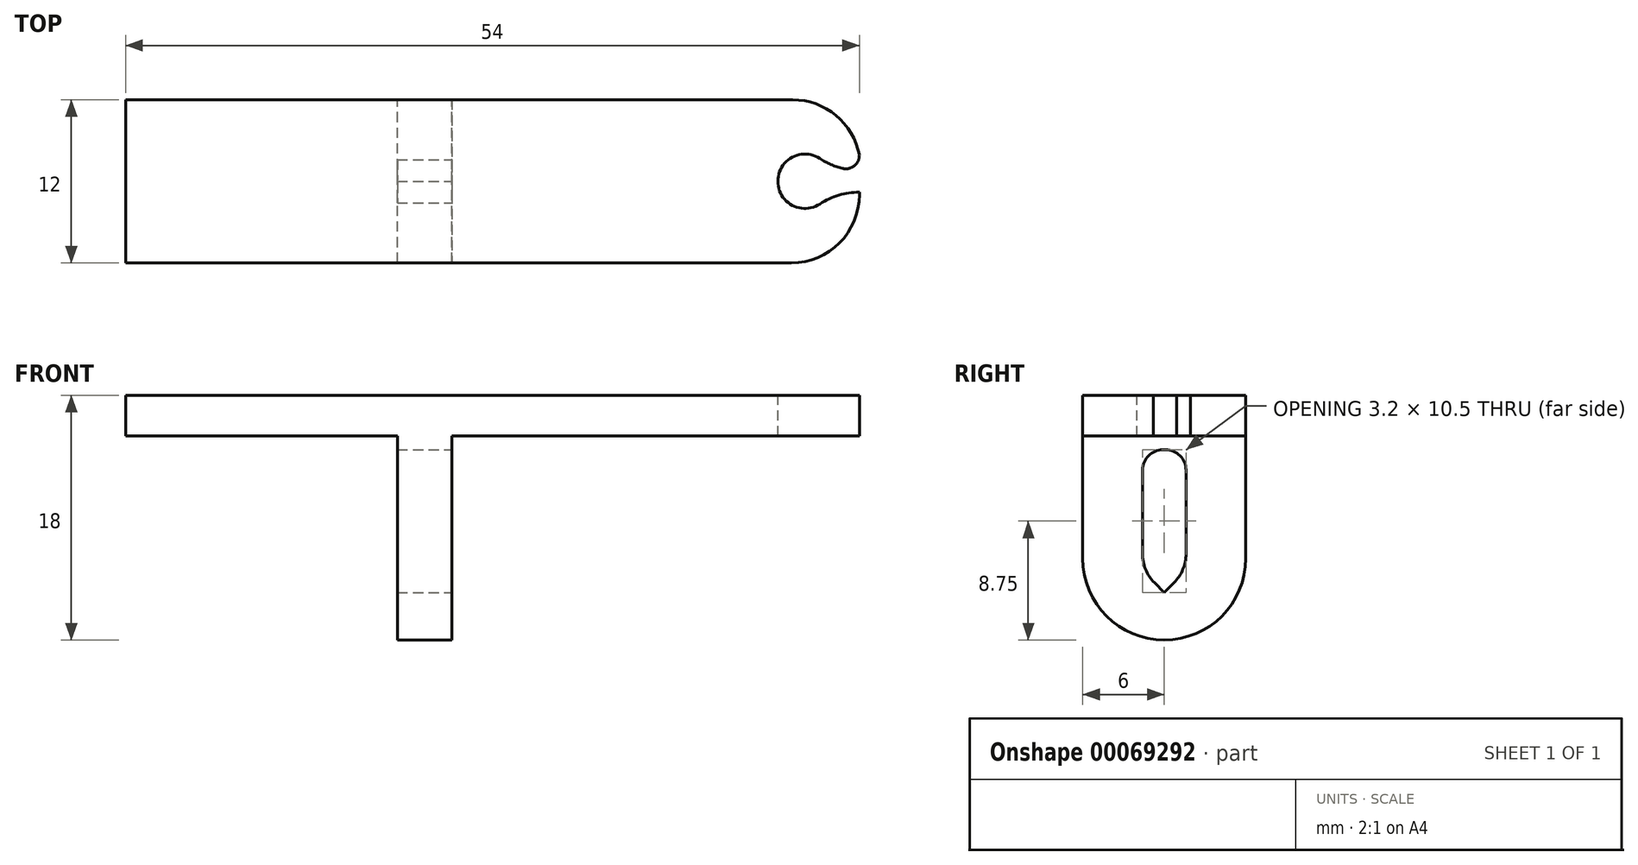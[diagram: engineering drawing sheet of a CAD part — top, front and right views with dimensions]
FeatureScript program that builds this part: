
annotation { "Feature Type Name" : "Feature", "Feature Type Description" : "" }
export const myFeature = defineFeature(function(context is Context, id is Id, definition is map)
    precondition{}
    {
        {
            var Q0;
            Q0=qCreatedBy(makeId("Front.planeOp"),FACE);
            var sketch = newSketch(context, id + "F0", { "sketchPlane" : qUnion([Q0])});
            skLineSegment(sketch, "E0", {"start": v(0, 0) * mm, "end": v(30, 0) * mm});
            skLineSegment(sketch, "E1", {"start": v(30, 0) * mm, "end": v(30, 3) * mm});
            skLineSegment(sketch, "E2", {"start": v(30, 3) * mm, "end": v(-24, 3) * mm});
            skLineSegment(sketch, "E3", {"start": v(-24, 3) * mm, "end": v(-24, 0) * mm});
            skLineSegment(sketch, "E4", {"start": v(-24, 0) * mm, "end": v(-4, 0) * mm});
            skLineSegment(sketch, "E5", {"start": v(-4, 0) * mm, "end": v(-4, -15) * mm});
            skLineSegment(sketch, "E6", {"start": v(-4, -15) * mm, "end": v(0, -15) * mm});
            skLineSegment(sketch, "E7", {"start": v(0, -15) * mm, "end": v(0, 0) * mm});
            skSolve(sketch);
        }
        {
            var Q0;
            Q0=makeQuery(id+"F0.imprint","IMPRINT",FACE,{"disambiguationData":[TD([[makeQuery(id+"F0.imprint","IMPRINT",EDGE,{"derivedFrom":sQuery(id+"F0.wireOp",EDGE,"E0")}),1.0]])]});
            extrude(context, id + "F1", {"entities" : qUnion([Q0]), "endBound" : BoundingType.SYMMETRIC, "depth" : 12 * mm});
        }
        {
            var Q0;
            Q0=makeQuery(id+"F1.opExtrude","SWEPT_FACE",FACE,{"disambiguationData":[OSD([sQuery(id+"F0.wireOp",EDGE,"E2")])]});
            var sketch = newSketch(context, id + "F2", { "sketchPlane" : qUnion([Q0])});
            skArc(sketch, "E8", {"start": v(27.1, 1.67) * mm, "mid": v(24, 0) * mm, "end": v(27.1, -1.67) * mm});
            skArc(sketch, "E9", {"start": v(27.1, 1.67) * mm, "mid": v(28.49, 1.02) * mm, "end": v(30, 0.8) * mm});
            skLineSegment(sketch, "E10.0", {"start": v(30, -0.8) * mm, "end": v(30, 0.8) * mm});
            skArc(sketch, "E11.MirrorCS", {"start": v(27.1, -1.67) * mm, "mid": v(28.49, -1.02) * mm, "end": v(30, -0.8) * mm});
            skPoint(sketch, "E12.orphan", {"position": v(30, 6) * mm});
            skPoint(sketch, "E13.orphan", {"position": v(30, -6) * mm});
            skSolve(sketch);
        }
        {
            var Q0;
            Q0=makeQuery(id+"F2.imprint","IMPRINT",FACE,{"disambiguationData":[TD([[makeQuery(id+"F2.imprint","IMPRINT",EDGE,{"derivedFrom":sQuery(id+"F2.wireOp",EDGE,"E8")}),1.0]])]});
            extrude(context, id + "F3", {"entities" : qUnion([Q0]), "operationType" : NewBodyOperationType.REMOVE, "endBound" : BoundingType.THROUGH_ALL, "oppositeDirection" : true, "depth" : 25 * mm});
        }
        {
            var Q0;
            Q0=makeQuery(id+"F3.boolean.opBoolean","COPY",EDGE,{"derivedFrom":makeQuery(id+"F3.opExtrude","SWEPT_EDGE",EDGE,{"disambiguationData":[OSD([sQuery(id+"F0.wireOp",EDGE,"E1"),sQuery(id+"F0.wireOp",EDGE,"E2"),sQuery(id+"F2.wireOp",EDGE,"E9"),sQuery(id+"F2.wireOp",EDGE,"E10.0")])]})});
            var Q1;
            Q1=makeQuery(id+"F3.boolean.opBoolean","COPY",EDGE,{"derivedFrom":makeQuery(id+"F3.opExtrude","SWEPT_EDGE",EDGE,{"disambiguationData":[OSD([sQuery(id+"F0.wireOp",EDGE,"E1"),sQuery(id+"F0.wireOp",EDGE,"E2"),sQuery(id+"F2.wireOp",EDGE,"E10.0"),sQuery(id+"F2.wireOp",EDGE,"E11.MirrorCS")])]})});
            fillet(context, id + "F4", {"entities" : qUnion([Q0, Q1]), "radius" : 1 * mm, "allowEdgeOverflow" : false});
        }
        {
            var Q0;
            Q0=makeQuery(id+"F1.opExtrude","CAP_EDGE",EDGE,{"disambiguationData":[OSD([sQuery(id+"F0.wireOp",EDGE,"E1")])],"isStart":true});
            var Q1;
            Q1=makeQuery(id+"F1.opExtrude","CAP_EDGE",EDGE,{"disambiguationData":[OSD([sQuery(id+"F0.wireOp",EDGE,"E1")])],"isStart":false});
            fillet(context, id + "F5", {"entities" : qUnion([Q0, Q1]), "radius" : 5 * mm, "tangentPropagation" : true, "allowEdgeOverflow" : false});
        }
        {
            var Q0;
            Q0=makeQuery(id+"F1.opExtrude","SWEPT_FACE",FACE,{"disambiguationData":[OSD([sQuery(id+"F0.wireOp",EDGE,"E7")])]});
            var sketch = newSketch(context, id + "F6", { "sketchPlane" : qUnion([Q0])});
            skLineSegment(sketch, "E14.rect.bottom", {"start": v(-0.1, -1) * mm, "end": v(0.1, -1) * mm});
            skLineSegment(sketch, "E14.rect.left", {"start": v(-1.6, -2.5) * mm, "end": v(-1.6, -9.9) * mm});
            skLineSegment(sketch, "E14.rect.right", {"start": v(1.6, -2.5) * mm, "end": v(1.6, -9.9) * mm});
            skPoint(sketch, "E15", {"position": v(0, -1) * mm});
            skPoint(sketch, "E16.visualSharp", {"position": v(-1.6, -1) * mm});
            skArc(sketch, "E16.filletArc", {"start": v(-0.1, -1) * mm, "mid": v(-1.16, -1.44) * mm, "end": v(-1.6, -2.5) * mm});
            skPoint(sketch, "E17.visualSharp", {"position": v(1.6, -1) * mm});
            skArc(sketch, "E17.filletArc", {"start": v(1.6, -2.5) * mm, "mid": v(1.16, -1.44) * mm, "end": v(0.1, -1) * mm});
            skLineSegment(sketch, "E18", {"start": v(0, -11.5) * mm, "end": v(-1.6, -9.9) * mm});
            skLineSegment(sketch, "E19", {"start": v(0, -11.5) * mm, "end": v(1.6, -9.9) * mm});
            skPoint(sketch, "E20.orphan", {"position": v(-1.6, -11.5) * mm});
            skPoint(sketch, "E21.orphan", {"position": v(1.6, -11.5) * mm});
            skSolve(sketch);
        }
        {
            var Q0;
            Q0=makeQuery(id+"F6.imprint","IMPRINT",FACE,{"disambiguationData":[TD([[makeQuery(id+"F6.imprint","IMPRINT",EDGE,{"derivedFrom":sQuery(id+"F6.wireOp",EDGE,"E14.rect.bottom")}),-1.0]])]});
            extrude(context, id + "F7", {"entities" : qUnion([Q0]), "operationType" : NewBodyOperationType.REMOVE, "endBound" : BoundingType.THROUGH_ALL, "oppositeDirection" : true, "depth" : 25 * mm});
        }
        {
            var Q0;
            Q0=makeQuery(id+"F7.boolean.opBoolean","COPY",EDGE,{"derivedFrom":makeQuery(id+"F7.opExtrude","SWEPT_EDGE",EDGE,{"disambiguationData":[OSD([sQuery(id+"F0.wireOp",EDGE,"E6"),sQuery(id+"F0.wireOp",EDGE,"E7"),sQuery(id+"F6.wireOp",EDGE,"E14.rect.top"),sQuery(id+"F6.wireOp",EDGE,"E14.rect.right")])]})});
            var Q1;
            Q1=makeQuery(id+"F7.boolean.opBoolean","COPY",EDGE,{"derivedFrom":makeQuery(id+"F7.opExtrude","SWEPT_EDGE",EDGE,{"disambiguationData":[OSD([sQuery(id+"F0.wireOp",EDGE,"E6"),sQuery(id+"F0.wireOp",EDGE,"E7"),sQuery(id+"F6.wireOp",EDGE,"E14.rect.top"),sQuery(id+"F6.wireOp",EDGE,"E14.rect.left")])]})});
            fillet(context, id + "F8", {"entities" : qUnion([Q0, Q1]), "radius" : 3 * mm, "tangentPropagation" : true, "allowEdgeOverflow" : false});
        }
        {
            var Q0;
            Q0=makeQuery(id+"F1.opExtrude","CAP_EDGE",EDGE,{"disambiguationData":[OSD([sQuery(id+"F0.wireOp",EDGE,"E6")])],"isStart":false});
            var Q1;
            Q1=makeQuery(id+"F1.opExtrude","CAP_EDGE",EDGE,{"disambiguationData":[OSD([sQuery(id+"F0.wireOp",EDGE,"E6")])],"isStart":true});
            fillet(context, id + "F9", {"entities" : qUnion([Q0, Q1]), "radius" : 6 * mm, "tangentPropagation" : true, "allowEdgeOverflow" : false});
        }
    });
